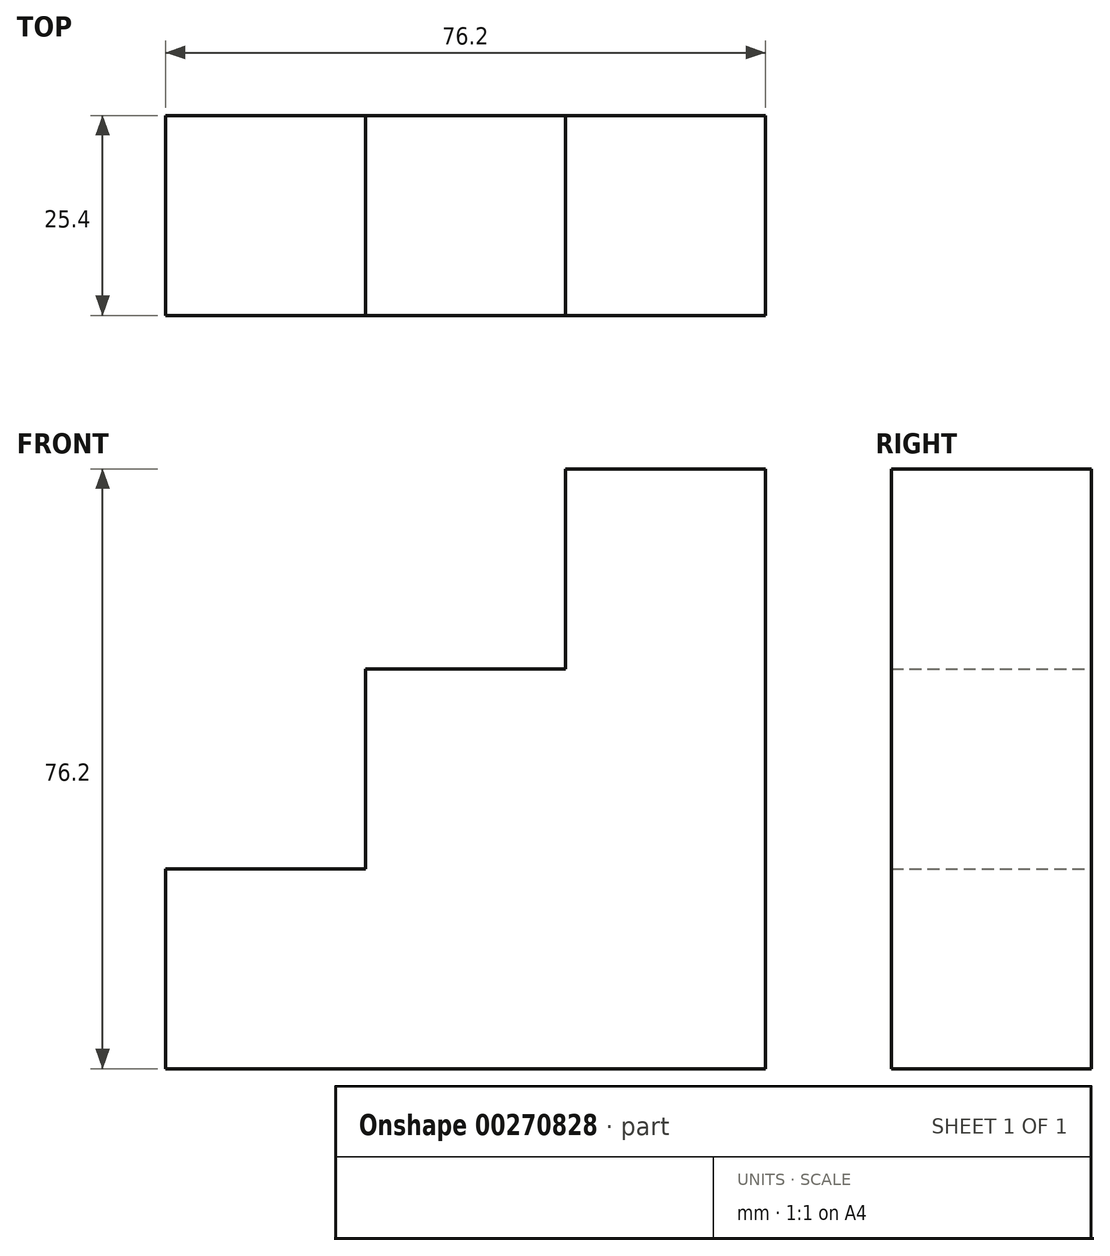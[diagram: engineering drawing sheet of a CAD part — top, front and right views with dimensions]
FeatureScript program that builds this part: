
annotation { "Feature Type Name" : "Feature", "Feature Type Description" : "" }
export const myFeature = defineFeature(function(context is Context, id is Id, definition is map)
    precondition{}
    {
        {
            var Q0;
            Q0=qCreatedBy(makeId("Front.planeOp"),FACE);
            var sketch = newSketch(context, id + "F0", { "sketchPlane" : qUnion([Q0])});
            skLineSegment(sketch, "E0", {"start": v(0, 0) * mm, "end": v(0, 76.2) * mm});
            skLineSegment(sketch, "E1", {"start": v(0, 76.2) * mm, "end": v(-25.4, 76.2) * mm});
            skLineSegment(sketch, "E2", {"start": v(-25.4, 76.2) * mm, "end": v(-25.4, 50.8) * mm});
            skLineSegment(sketch, "E3", {"start": v(-25.4, 50.8) * mm, "end": v(-50.8, 50.8) * mm});
            skLineSegment(sketch, "E4", {"start": v(-50.8, 50.8) * mm, "end": v(-50.8, 25.4) * mm});
            skLineSegment(sketch, "E5", {"start": v(-50.8, 25.4) * mm, "end": v(-76.2, 25.4) * mm});
            skLineSegment(sketch, "E6", {"start": v(-76.2, 25.4) * mm, "end": v(-76.2, 0) * mm});
            skLineSegment(sketch, "E7", {"start": v(-76.2, 0) * mm, "end": v(0, 0) * mm});
            skSolve(sketch);
        }
        {
            var Q0;
            Q0 = qSketchRegion(id + "F0", true);
            extrude(context, id + "F1", {"entities" : qUnion([Q0]), "depth" : 25.4 * mm});
        }
    });
